# Revit family: 797280001_LLAVE JARDÍN LIVIANA BRONCE
name_source: partatom
category: Plumbing Fixtures
units: mm (PartAtom-declared; Revit-internal decimal feet)

## family parameters
Always vertical = Yes
Cut with Voids When Loaded = No
OmniClass Number = 23.31.11.13.11
OmniClass Title = Sink Compression Faucets
Part Type = Normal
Room Calculation Point = No
Round Connector Dimension = Use Diameter
Shared = No
Work Plane-Based = No

## types (1)
- 797280001_LLAVE JARDÍN LIVIANA BRONCE
    Capacidad de flujo estimada real a 20 psi = 31,86 L/min
    Ciclo de vida de unidad de cierre = 500.000 ciclos
    Color = Bronce
    Creado por = IDD
    Description = Llave jardín acabado bronce, sistema de cierre de alto desempeño

Garantía por 30 años
    Dimensiones generales del producto = (H x W x L): 68 x 27 x 101 mm, (H x W x L): 2,7 x 1,1 x 4,0 pulg
    Fecha de creación = 4/08/2020
    Material = Corona_Laton_Cobre
    Material específico = Latón
    Materiales = Metálico
    Peso bruto = 200 gr. - 0,44 lb
    Peso neto = 178 gr. - 0,39 lb
    Presión máxima recomendada = 125 psi
    Presión mínima recomendada = 20 psi
    REFERENCIAS DEL PRODCUTO 1 = 797280001 LLAVE JRD CORR 1/2P SALI 3/4P BRONCE
    REFERENCIAS DEL PRODCUTO 2 = 797285551 LLAVE JRD 1/2P- 3/4P BRONCE M12 CP6
    REFERENCIAS DEL PRODCUTO 3 = 797283331 LLAVE JRD CORR 1/2P SALI 3/4P BRONCEX6
    Temperatura máxima de trabajo = 71˚C - 159,8˚F
    Temperatura mínima de trabajo = 5˚C - 41˚F
    URL = https://www.grival.com

## geometry (parser evidence)
native form markers: Sweep x5
no freeform markers — native parametric forms only
